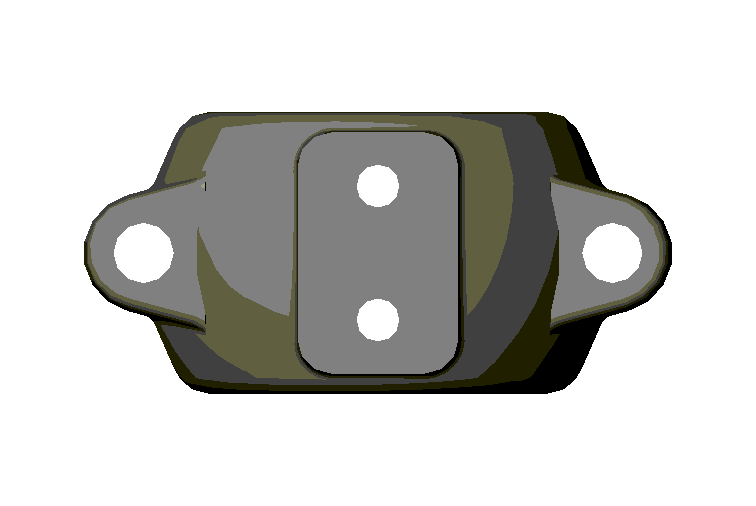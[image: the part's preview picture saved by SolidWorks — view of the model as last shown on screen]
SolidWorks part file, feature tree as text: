
SOLIDWORKS PART (.sldprt)
format: sldprt  version: not decoded by parser v0  size: 289,280 bytes
history: native  units: mm
features: sketch x7, plane x4, cut_extrude x4, fillet x4, extrude x2, material x1, revolve x1 + 1 further entry (+7 scaffold rows collapsed)
feature tree (31):
  scaffold x7  (default folders/planes/origin — collapsed)
  material  "Matériau <non spécifié>"
  "Corps de surface"
  plane  "Plan1"
  plane  "Plan2"
  plane  "Plan3"
  sketch  "Esquisse4"  dims[D1=70.0mm D3=18.0mm D5=5.0mm D2=42.0mm D4=70.0mm]
  revolve  "Base-Révolution"  Angle=180deg
  sketch  "Esquisse5"  dims[c1.D1=~10.825999mm c2.D1=~21.048663deg c3.D1=~10.825999mm c4.D1=~21.048663deg c5.D1=~21.651997mm c5.D2=70.0mm c5.D3=~20.841683mm c6.D3=15.0deg c6.D4=~28.82137mm c7.D4=15.0deg c7.D5=~23.551369mm c8.D5=15.0deg c8.D6=~15.753472mm c9.D6=15.0deg]
  extrude  "Boss.-Extru.1"  Depth=22mm
  sketch  "Esquisse7"  dims[D1=9.0mm D2=9.0mm D3=~12.167413mm]
  cut_extrude  "Enlèv. mat.-Extru.2"  [1 undecoded]
  fillet  "Congé2"  Radius=2mm
  fillet  "Congé3"  Radius=2mm
  plane  "Plan4"  Offset=39mm
  sketch  "Esquisse8"  dims[D5=5.0mm D1=24.0mm D2=36.0mm D3=18.0mm D4=12.0mm]
  extrude  "Boss.-Extru.2"  [1 undecoded]
  fillet  "Congé4"  Radius=2mm
  sketch  "Esquisse9"  dims[D1=6.4mm D2=20.0mm]
  cut_extrude  "Enlèv. mat.-Extru.3"  [1 undecoded]
  sketch  "Esquisse10"  dims[c1.D1=~13.416408mm c1.D2=~14.56022mm c2.D1=16.0mm c2.D2=16.0mm]
  cut_extrude  "Enlèv. mat.-Extru.4"  Depth=27mm
  sketch  "Esquisse11"  dims[D1=12.0mm]
  cut_extrude  "Enlèv. mat.-Extru.5"  Depth=7mm
  fillet  "Congé6"  Radius=2mm
decode coverage: 15 of 18 modeling features carry decoded parameters; 1 rows unclassified (native names shown)
note: ~ marks probable driven/reference dimensions
note: 3 parameter values undecoded
summary: no parameter record found for 3 features
note: suppression state not decoded; provenance and decode notes live in map.json
